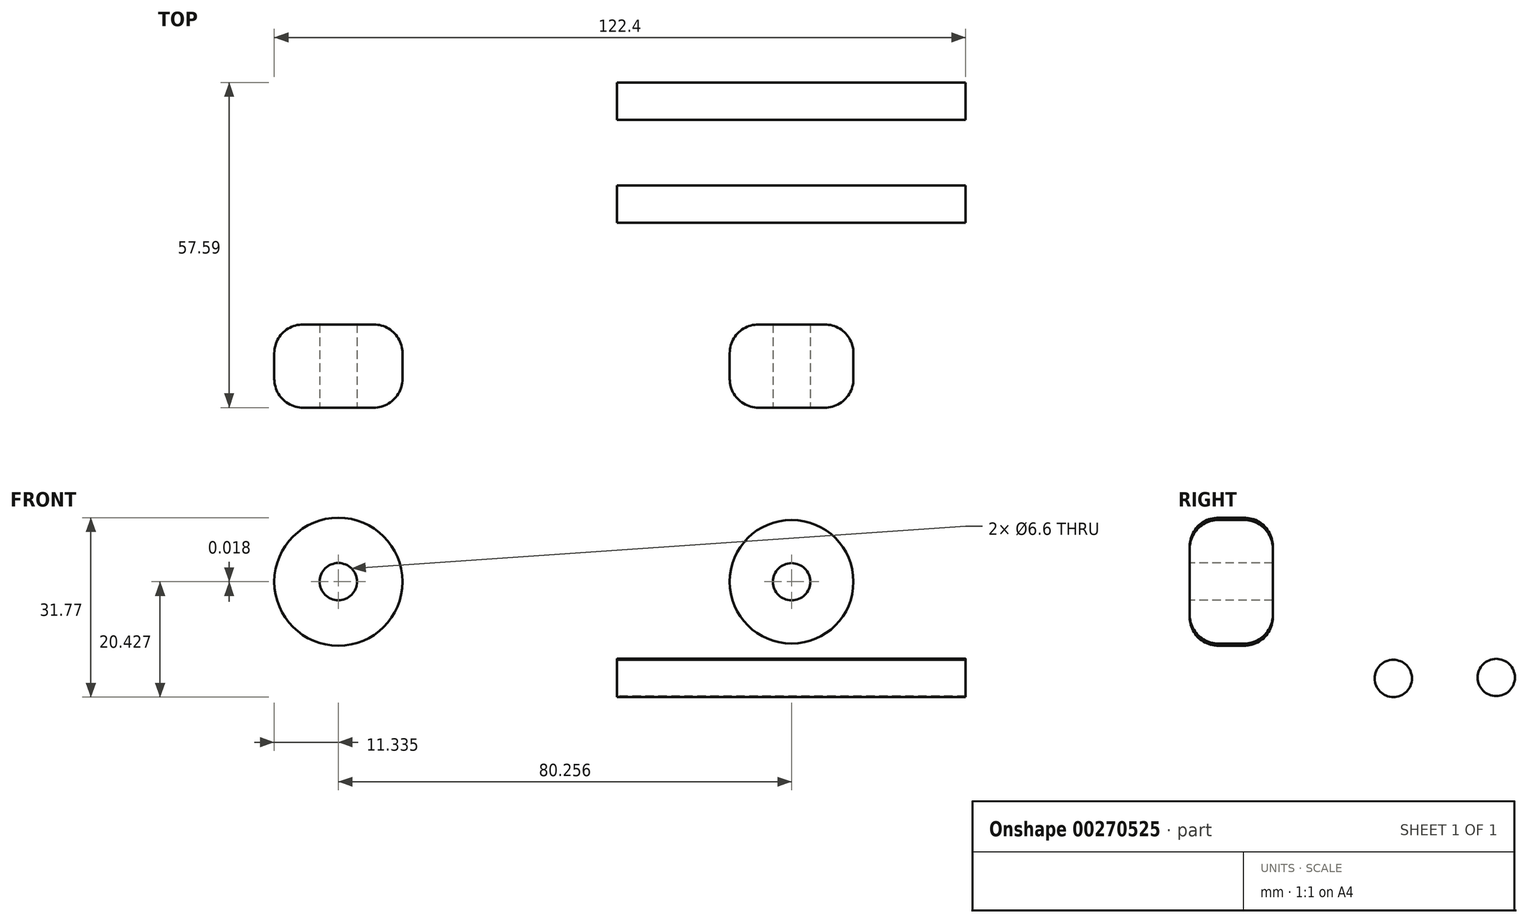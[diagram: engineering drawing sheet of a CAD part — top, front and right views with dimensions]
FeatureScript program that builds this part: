
annotation { "Feature Type Name" : "Feature", "Feature Type Description" : "" }
export const myFeature = defineFeature(function(context is Context, id is Id, definition is map)
    precondition{}
    {
        {
            var Q0;
            Q0=qCreatedBy(makeId("Front.planeOp"),FACE);
            var sketch = newSketch(context, id + "F0", { "sketchPlane" : qUnion([Q0])});
            skCircle(sketch, "E0", {"center": v(-49.34, 47.26) * mm, "radius": 11.34 * mm});
            skCircle(sketch, "E1", {"center": v(30.91, 47.26) * mm, "radius": 10.95 * mm});
            skSolve(sketch);
        }
        {
            var Q0;
            Q0=makeQuery(id+"F0.imprint","IMPRINT",FACE,{"disambiguationData":[TD([[makeQuery(id+"F0.imprint","IMPRINT",EDGE,{"derivedFrom":sQuery(id+"F0.wireOp",EDGE,"E0")}),1.0]])]});
            var Q1;
            Q1=makeQuery(id+"F0.imprint","IMPRINT",FACE,{"disambiguationData":[TD([[makeQuery(id+"F0.imprint","IMPRINT",EDGE,{"derivedFrom":sQuery(id+"F0.wireOp",EDGE,"E1")}),1.0]])]});
            extrude(context, id + "F1", {"entities" : qUnion([Q0, Q1]), "depth" : 14.73 * mm});
        }
        {
            var Q0;
            Q0=makeQuery(id+"F1.opExtrude","CAP_EDGE",EDGE,{"disambiguationData":[OSD([sQuery(id+"F0.wireOp",EDGE,"E1")])],"isStart":false});
            var Q1;
            Q1=makeQuery(id+"F1.opExtrude","CAP_EDGE",EDGE,{"disambiguationData":[OSD([sQuery(id+"F0.wireOp",EDGE,"E1")])],"isStart":true});
            var Q2;
            Q2=makeQuery(id+"F1.opExtrude","CAP_EDGE",EDGE,{"disambiguationData":[OSD([sQuery(id+"F0.wireOp",EDGE,"E0")])],"isStart":true});
            var Q3;
            Q3=makeQuery(id+"F1.opExtrude","CAP_EDGE",EDGE,{"disambiguationData":[OSD([sQuery(id+"F0.wireOp",EDGE,"E0")])],"isStart":false});
            fillet(context, id + "F2", {"entities" : qUnion([Q0, Q1, Q2, Q3]), "radius" : 5.08 * mm, "tangentPropagation" : true, "allowEdgeOverflow" : false});
        }
        {
            var Q0;
            Q0=qCreatedBy(makeId("Right.planeOp"),FACE);
            var sketch = newSketch(context, id + "F3", { "sketchPlane" : qUnion([Q0])});
            skCircle(sketch, "E2", {"center": v(21.33, 30.13) * mm, "radius": 3.3 * mm});
            skCircle(sketch, "E3", {"center": v(39.55, 30.3) * mm, "radius": 3.3 * mm});
            skSolve(sketch);
        }
        {
            var Q0;
            Q0=makeQuery(id+"F3.imprint","IMPRINT",FACE,{"disambiguationData":[TD([[makeQuery(id+"F3.imprint","IMPRINT",EDGE,{"derivedFrom":sQuery(id+"F3.wireOp",EDGE,"E2")}),1.0]])]});
            var Q1;
            Q1=makeQuery(id+"F3.imprint","IMPRINT",FACE,{"disambiguationData":[TD([[makeQuery(id+"F3.imprint","IMPRINT",EDGE,{"derivedFrom":sQuery(id+"F3.wireOp",EDGE,"E3")}),1.0]])]});
            extrude(context, id + "F4", {"entities" : qUnion([Q0, Q1]), "depth" : 61.72 * mm});
        }
        {
            var Q0;
            Q0=makeQuery(id+"F1.opExtrude","CAP_FACE",FACE,{"disambiguationData":[OSD([sQuery(id+"F0.wireOp",EDGE,"E1")])],"isStart":false});
            var sketch = newSketch(context, id + "F5", { "sketchPlane" : qUnion([Q0])});
            skPoint(sketch, "E4", {"position": v(30.91, 47.26) * mm});
            skSolve(sketch);
        }
        {
            var Q0;
            Q0=makeQuery(id+"F1.opExtrude","CAP_FACE",FACE,{"disambiguationData":[OSD([sQuery(id+"F0.wireOp",EDGE,"E0")])],"isStart":false});
            var sketch = newSketch(context, id + "F6", { "sketchPlane" : qUnion([Q0])});
            skPoint(sketch, "E5", {"position": v(-49.35, 47.28) * mm});
            skSolve(sketch);
        }
        {
            var Q0;
            Q0=sQuery(id+"F6.wireOp",VERTEX,"E5");
            var Q1;
            Q1=makeQuery(id+"F1.opExtrude","SWEPT_BODY",BODY,{"disambiguationData":[OSD([sQuery(id+"F0.wireOp",EDGE,"E0")])]});
            hole(context, id + "F7", {"style" : HoleStyle.SIMPLE, "endStyle" : HoleEndStyle.BLIND, "holeDiameter" : 6.6 * mm, "holeDepth" : 50.8 * mm, "tappedDepth" : 12.7 * mm, "tapClearance" : 3, "locations" : qUnion([Q0]), "scope" : qUnion([Q1])});
        }
        {
            var Q0;
            Q0=sQuery(id+"F5.wireOp",VERTEX,"E4");
            var Q1;
            Q1=makeQuery(id+"F1.opExtrude","SWEPT_BODY",BODY,{"disambiguationData":[OSD([sQuery(id+"F0.wireOp",EDGE,"E1")])]});
            hole(context, id + "F8", {"style" : HoleStyle.SIMPLE, "endStyle" : HoleEndStyle.BLIND, "holeDiameter" : 6.6 * mm, "holeDepth" : 50.8 * mm, "tappedDepth" : 12.7 * mm, "tapClearance" : 3, "locations" : qUnion([Q0]), "scope" : qUnion([Q1])});
        }
    });
